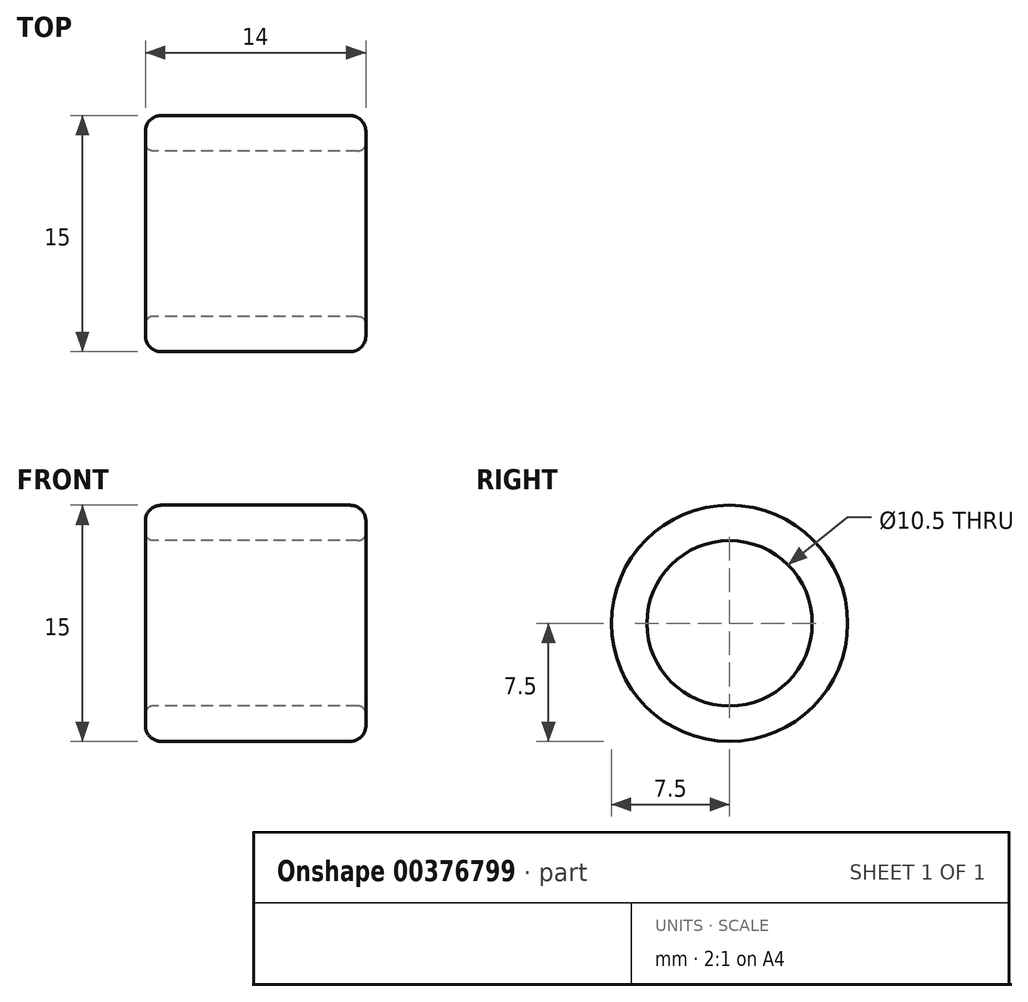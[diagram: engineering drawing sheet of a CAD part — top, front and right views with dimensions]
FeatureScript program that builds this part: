
annotation { "Feature Type Name" : "Feature", "Feature Type Description" : "" }
export const myFeature = defineFeature(function(context is Context, id is Id, definition is map)
    precondition{}
    {
        {
            var Q0;
            Q0=qCreatedBy(makeId("Right.planeOp"),FACE);
            var sketch = newSketch(context, id + "F0", { "sketchPlane" : qUnion([Q0])});
            skCircle(sketch, "E0", {"center": v(0, 0) * mm, "radius": 7.5 * mm});
            skCircle(sketch, "E1", {"center": v(0, 0) * mm, "radius": 5.25 * mm});
            skSolve(sketch);
        }
        {
            var Q0;
            Q0 = qSketchRegion(id + "F0", true);
            extrude(context, id + "F1", {"entities" : qUnion([Q0]), "depth" : 14 * mm});
        }
        {
            var Q0;
            Q0=makeQuery(id+"F1.opExtrude","CAP_EDGE",EDGE,{"disambiguationData":[OSD([sQuery(id+"F0.wireOp",EDGE,"E0")])],"isStart":true});
            var Q1;
            Q1=makeQuery(id+"F1.opExtrude","CAP_EDGE",EDGE,{"disambiguationData":[OSD([sQuery(id+"F0.wireOp",EDGE,"E0")])],"isStart":false});
            fillet(context, id + "F2", {"entities" : qUnion([Q0, Q1]), "radius" : 1 * mm, "tangentPropagation" : true, "allowEdgeOverflow" : false});
        }
        {
            var Q0;
            Q0=makeQuery(id+"F1.opExtrude","CAP_EDGE",EDGE,{"disambiguationData":[OSD([sQuery(id+"F0.wireOp",EDGE,"E1")])],"isStart":false});
            var Q1;
            Q1=makeQuery(id+"F1.opExtrude","SWEPT_FACE",FACE,{"disambiguationData":[OSD([sQuery(id+"F0.wireOp",EDGE,"E1")])]});
            fillet(context, id + "F3", {"entities" : qUnion([Q0, Q1]), "radius" : 0.5 * mm, "tangentPropagation" : true, "allowEdgeOverflow" : false});
        }
    });
